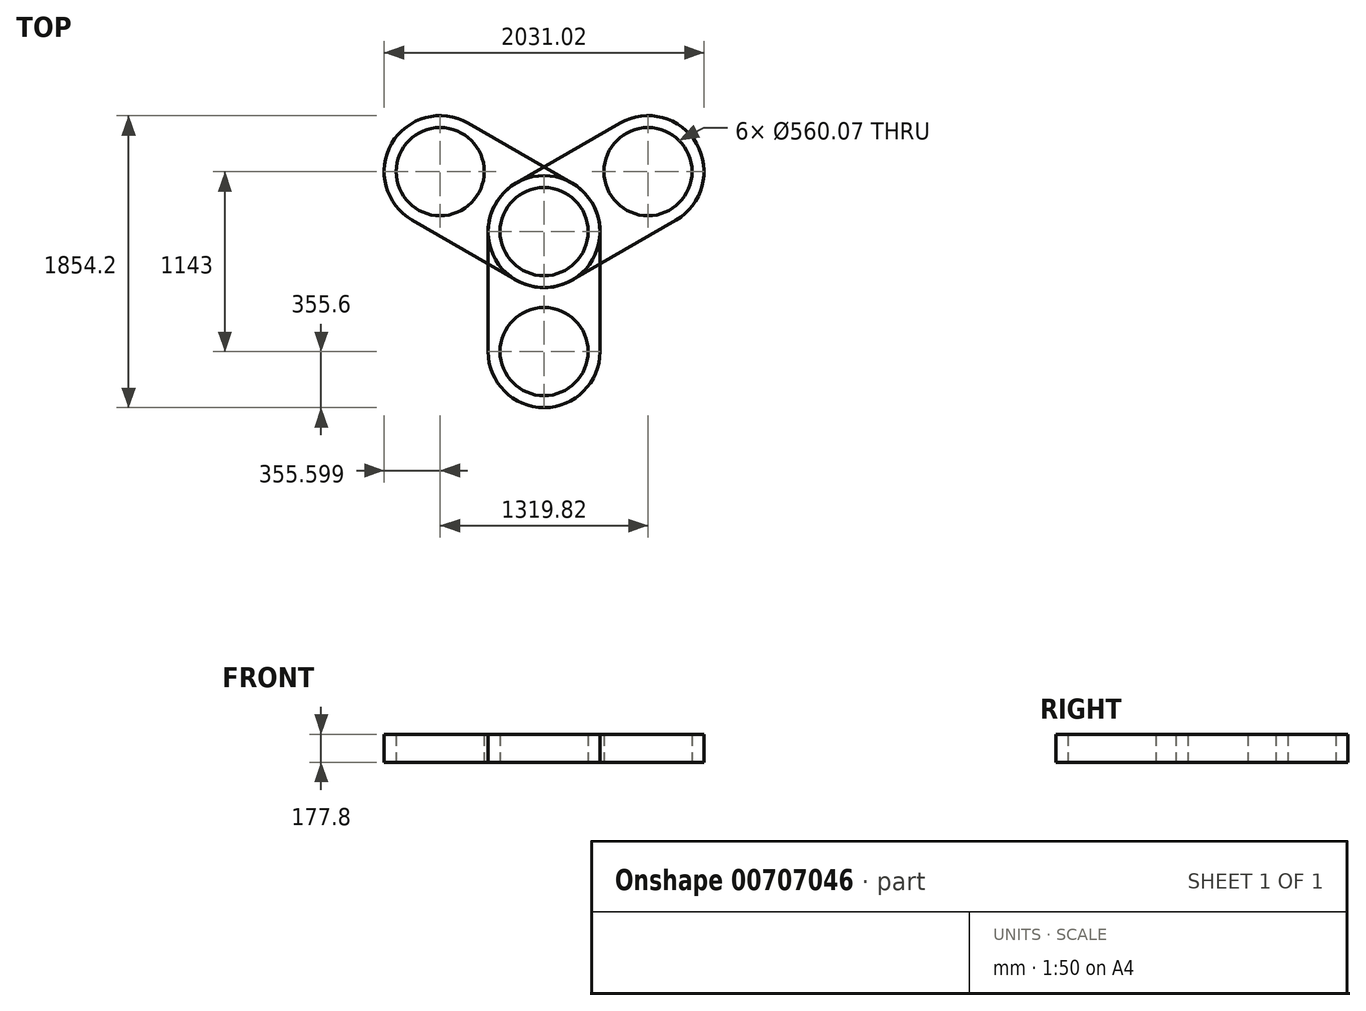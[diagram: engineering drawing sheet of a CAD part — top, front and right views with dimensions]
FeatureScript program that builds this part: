
annotation { "Feature Type Name" : "Feature", "Feature Type Description" : "" }
export const myFeature = defineFeature(function(context is Context, id is Id, definition is map)
    precondition{}
    {
        {
            var Q0;
            Q0=qCreatedBy(makeId("Top.planeOp"),FACE);
            var sketch = newSketch(context, id + "F0", { "sketchPlane" : qUnion([Q0])});
            skLineSegment(sketch, "E0.bottom", {"start": v(0, 0) * mm, "end": v(711.2, 0) * mm});
            skLineSegment(sketch, "E0.top", {"start": v(0, 762) * mm, "end": v(711.2, 762) * mm});
            skLineSegment(sketch, "E0.left", {"start": v(0, 0) * mm, "end": v(0, 762) * mm});
            skLineSegment(sketch, "E0.right", {"start": v(711.2, 0) * mm, "end": v(711.2, 762) * mm});
            skCircle(sketch, "E1", {"center": v(355.6, 762) * mm, "radius": 355.6 * mm});
            skCircle(sketch, "E2", {"center": v(355.6, 762) * mm, "radius": 280.04 * mm});
            skCircle(sketch, "E3", {"center": v(355.6, 0) * mm, "radius": 355.6 * mm});
            skCircle(sketch, "E4", {"center": v(355.6, 0) * mm, "radius": 280.04 * mm});
            skSolve(sketch);
        }
        {
            var Q0;
            {var subQ1=sQuery(id+"F0.wireOp",EDGE,"E0.bottom");var subQ3=sQuery(id+"F0.wireOp",EDGE,"E4");var subQ4=makeQuery(id+"F0.imprint","INTERSECT",VERTEX,{"disambiguationData":[OD(0.0)],"derivedFrom":[subQ1,subQ3]});Q0=makeQuery(id+"F0.imprint","IMPRINT",FACE,{"disambiguationData":[TD([[makeQuery(id+"F0.imprint","IMPRINT",EDGE,{"disambiguationData":[TD([[subQ4,-1.0]])],"derivedFrom":subQ3}),-1.0]])]});}
            var Q1;
            {var subQ1=sQuery(id+"F0.wireOp",EDGE,"E0.bottom");var subQ3=sQuery(id+"F0.wireOp",EDGE,"E4");var subQ4=makeQuery(id+"F0.imprint","INTERSECT",VERTEX,{"disambiguationData":[OD(0.0)],"derivedFrom":[subQ1,subQ3]});Q1=makeQuery(id+"F0.imprint","IMPRINT",FACE,{"disambiguationData":[TD([[makeQuery(id+"F0.imprint","IMPRINT",EDGE,{"disambiguationData":[TD([[subQ4,1.0]])],"derivedFrom":subQ3}),-1.0]])]});}
            var Q2;
            {var subQ0=sQuery(id+"F0.wireOp",EDGE,"E0.left");Q2=makeQuery(id+"F0.imprint","IMPRINT",FACE,{"disambiguationData":[TD([[makeQuery(id+"F0.imprint","IMPRINT",EDGE,{"derivedFrom":subQ0}),-1.0]])]});}
            var Q3;
            {var subQ1=sQuery(id+"F0.wireOp",EDGE,"E0.top");var subQ3=sQuery(id+"F0.wireOp",EDGE,"E2");var subQ4=makeQuery(id+"F0.imprint","INTERSECT",VERTEX,{"disambiguationData":[OD(0.0)],"derivedFrom":[subQ1,subQ3]});Q3=makeQuery(id+"F0.imprint","IMPRINT",FACE,{"disambiguationData":[TD([[makeQuery(id+"F0.imprint","IMPRINT",EDGE,{"disambiguationData":[TD([[subQ4,1.0]])],"derivedFrom":subQ3}),-1.0]])]});}
            var Q4;
            {var subQ1=sQuery(id+"F0.wireOp",EDGE,"E0.top");var subQ3=sQuery(id+"F0.wireOp",EDGE,"E2");var subQ4=makeQuery(id+"F0.imprint","INTERSECT",VERTEX,{"disambiguationData":[OD(0.0)],"derivedFrom":[subQ1,subQ3]});Q4=makeQuery(id+"F0.imprint","IMPRINT",FACE,{"disambiguationData":[TD([[makeQuery(id+"F0.imprint","IMPRINT",EDGE,{"disambiguationData":[TD([[subQ4,-1.0]])],"derivedFrom":subQ3}),-1.0]])]});}
            extrude(context, id + "F1", {"entities" : qUnion([Q0, Q1, Q2, Q3, Q4]), "depth" : 177.8 * mm, "offsetDistance" : 25.4 * mm});
        }
        {
            var Q0;
            Q0=makeQuery(id+"F1.opExtrude","SWEPT_BODY",BODY,{"disambiguationData":[OSD([sQuery(id+"F0.wireOp",EDGE,"E0.left"),sQuery(id+"F0.wireOp",EDGE,"E0.right"),sQuery(id+"F0.wireOp",EDGE,"E1"),sQuery(id+"F0.wireOp",EDGE,"E2"),sQuery(id+"F0.wireOp",EDGE,"E3"),sQuery(id+"F0.wireOp",EDGE,"E4")])]});
            var Q1;
            Q1=makeQuery(id+"F1.opExtrude","SWEPT_FACE",FACE,{"disambiguationData":[OSD([sQuery(id+"F0.wireOp",EDGE,"E1")])]});
            circularPattern(context, id + "F2", {"entities" : qUnion([Q0]), "axis" : qUnion([Q1]), "angle" : 360 * degree, "instanceCount" : 3, "equalSpace" : true});
        }
    });
